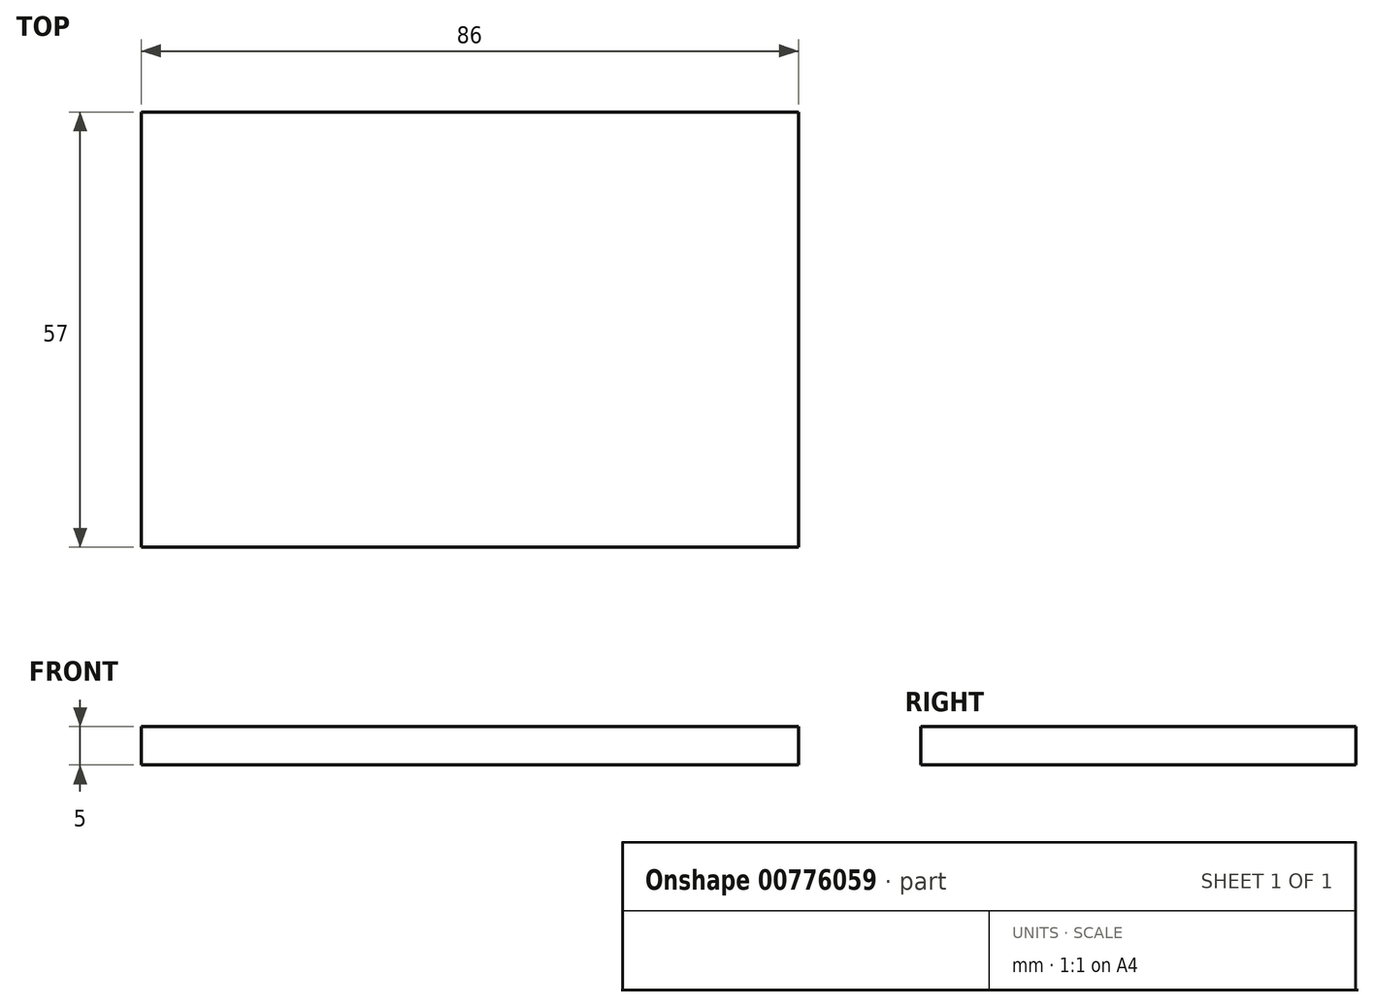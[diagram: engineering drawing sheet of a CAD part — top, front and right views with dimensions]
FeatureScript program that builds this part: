
annotation { "Feature Type Name" : "Feature", "Feature Type Description" : "" }
export const myFeature = defineFeature(function(context is Context, id is Id, definition is map)
    precondition{}
    {
        {
            var Q0;
            Q0=qCreatedBy(makeId("Top.planeOp"),FACE);
            var sketch = newSketch(context, id + "F0", { "sketchPlane" : qUnion([Q0])});
            skLineSegment(sketch, "E0.bottom", {"start": v(-43, 28.5) * mm, "end": v(43, 28.5) * mm});
            skLineSegment(sketch, "E0.top", {"start": v(-43, -28.5) * mm, "end": v(43, -28.5) * mm});
            skLineSegment(sketch, "E0.left", {"start": v(-43, 28.5) * mm, "end": v(-43, -28.5) * mm});
            skLineSegment(sketch, "E0.right", {"start": v(43, 28.5) * mm, "end": v(43, -28.5) * mm});
            skPoint(sketch, "E0.middle", {"position": v(0, 0) * mm});
            skSolve(sketch);
        }
        {
            var Q0;
            Q0=makeQuery(id+"F0.imprint","IMPRINT",FACE,{"disambiguationData":[TD([[makeQuery(id+"F0.imprint","IMPRINT",EDGE,{"derivedFrom":sQuery(id+"F0.wireOp",EDGE,"E0.bottom")}),-1.0]])]});
            extrude(context, id + "F1", {"entities" : qUnion([Q0]), "endBound" : BoundingType.SYMMETRIC, "depth" : 5 * mm, "offsetDistance" : 25 * mm});
        }
    });
